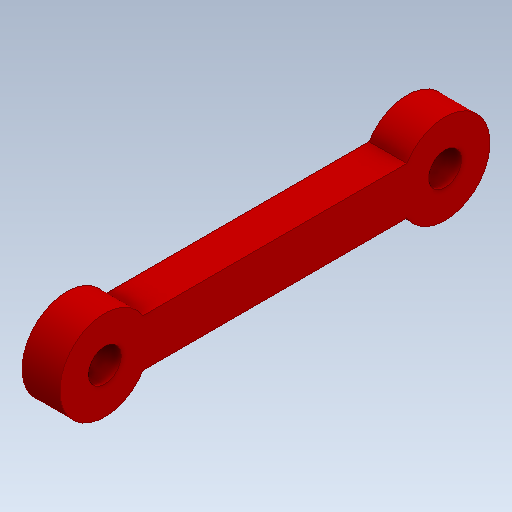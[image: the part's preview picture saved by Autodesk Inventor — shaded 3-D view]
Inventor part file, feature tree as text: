
AUTODESK INVENTOR PART (.ipt)
format: ipt  version: 2020 (Build 240168000, 168)  size: 121,344 bytes
history: native  units: in
note: dims shown in document units (in); Inventor stores cm internally (conversion verified against a paired STEP export)
features: extrude x1, sketch x1
ambient origin geometry x8: Origin, YZ Plane, XZ Plane, XY Plane, X Axis, Y Axis, Z Axis, Center Point
bodies: Solid1 (feature_tree)
feature tree (2):
  extrude  "Extrusion1"  Depth=1.4173in
  sketch  "Sketch1"  dims[d0=0.1378in d1=1.4173in d2=0.1181in d3=0.1181in d4=0.1969in d5=0.1575in d6=0.0in]
